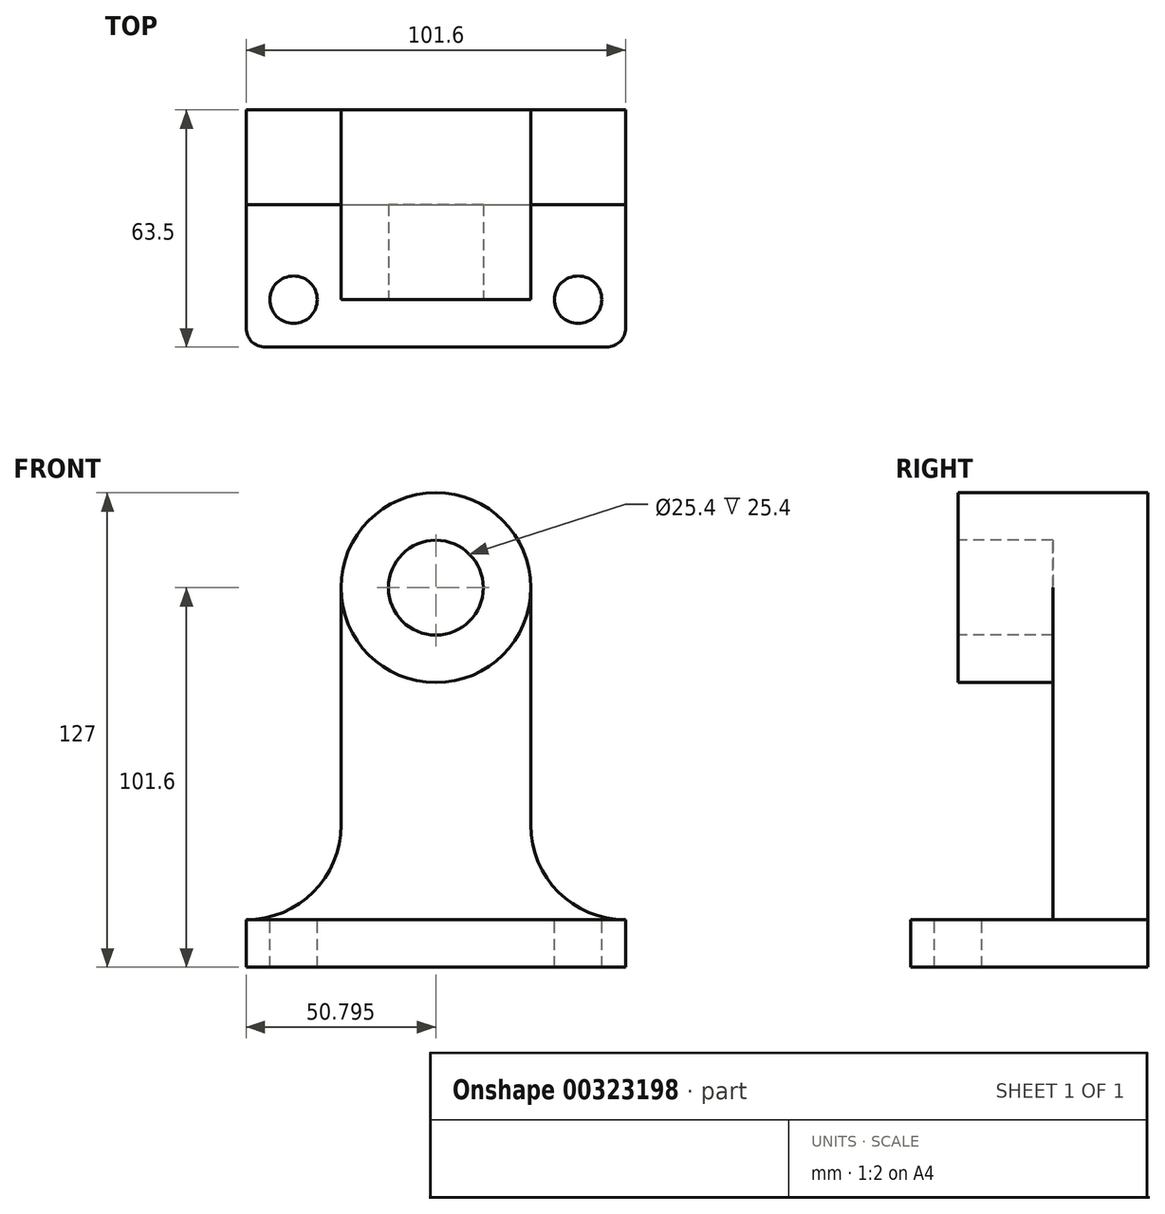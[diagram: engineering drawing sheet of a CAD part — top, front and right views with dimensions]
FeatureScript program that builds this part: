
annotation { "Feature Type Name" : "Feature", "Feature Type Description" : "" }
export const myFeature = defineFeature(function(context is Context, id is Id, definition is map)
    precondition{}
    {
        {
            var Q0;
            Q0=qCreatedBy(makeId("Top.planeOp"),FACE);
            var sketch = newSketch(context, id + "F0", { "sketchPlane" : qUnion([Q0])});
            skLineSegment(sketch, "E0", {"start": v(-42.13, 38.8) * mm, "end": v(59.47, 38.8) * mm});
            skLineSegment(sketch, "E1", {"start": v(59.47, 38.8) * mm, "end": v(59.47, -24.7) * mm});
            skLineSegment(sketch, "E2", {"start": v(59.47, -24.7) * mm, "end": v(-42.13, -24.7) * mm});
            skLineSegment(sketch, "E3", {"start": v(-42.13, -24.7) * mm, "end": v(-42.13, 38.8) * mm});
            skSolve(sketch);
        }
        {
            var Q0;
            Q0=makeQuery(id+"F0.imprint","IMPRINT",FACE,{"disambiguationData":[TD([[makeQuery(id+"F0.imprint","IMPRINT",EDGE,{"derivedFrom":sQuery(id+"F0.wireOp",EDGE,"E0")}),-1.0]])]});
            extrude(context, id + "F1", {"entities" : qUnion([Q0]), "depth" : 12.7 * mm});
        }
        {
            var Q0;
            Q0=makeQuery(id+"F1.opExtrude","SWEPT_EDGE",EDGE,{"disambiguationData":[OSD([sQuery(id+"F0.wireOp",EDGE,"E1"),sQuery(id+"F0.wireOp",EDGE,"E2")])]});
            var Q1;
            Q1=makeQuery(id+"F1.opExtrude","SWEPT_EDGE",EDGE,{"disambiguationData":[OSD([sQuery(id+"F0.wireOp",EDGE,"E2"),sQuery(id+"F0.wireOp",EDGE,"E3")])]});
            fillet(context, id + "F2", {"entities" : qUnion([Q0, Q1]), "radius" : 5.08 * mm, "tangentPropagation" : true, "allowEdgeOverflow" : false});
        }
        {
            var Q0;
            Q0=makeQuery(id+"F1.opExtrude","CAP_FACE",FACE,{"disambiguationData":[OSD([sQuery(id+"F0.wireOp",EDGE,"E0"),sQuery(id+"F0.wireOp",EDGE,"E1"),sQuery(id+"F0.wireOp",EDGE,"E2"),sQuery(id+"F0.wireOp",EDGE,"E3")])],"isStart":false});
            var sketch = newSketch(context, id + "F3", { "sketchPlane" : qUnion([Q0])});
            skLineSegment(sketch, "E4", {"start": v(-42.13, 38.8) * mm, "end": v(-42.13, 13.4) * mm});
            skLineSegment(sketch, "E5", {"start": v(59.47, 13.4) * mm, "end": v(59.47, 38.8) * mm});
            skLineSegment(sketch, "E6", {"start": v(59.47, 38.8) * mm, "end": v(-42.13, 38.8) * mm});
            skLineSegment(sketch, "E7", {"start": v(-42.13, 13.4) * mm, "end": v(59.47, 13.4) * mm});
            skSolve(sketch);
        }
        {
            var Q0;
            Q0=makeQuery(id+"F3.imprint","IMPRINT",FACE,{"disambiguationData":[TD([[makeQuery(id+"F3.imprint","IMPRINT",EDGE,{"derivedFrom":sQuery(id+"F3.wireOp",EDGE,"E4")}),-1.0]])]});
            extrude(context, id + "F4", {"entities" : qUnion([Q0]), "operationType" : NewBodyOperationType.ADD, "depth" : 63.5 * mm});
        }
        {
            var Q0;
            Q0=makeQuery(id+"F4.opExtrude","CAP_FACE",FACE,{"disambiguationData":[OSD([sQuery(id+"F3.wireOp",EDGE,"E4"),sQuery(id+"F3.wireOp",EDGE,"E5"),sQuery(id+"F3.wireOp",EDGE,"E6"),sQuery(id+"F3.wireOp",EDGE,"E7")])],"isStart":false});
            var sketch = newSketch(context, id + "F5", { "sketchPlane" : qUnion([Q0])});
            skLineSegment(sketch, "E8", {"start": v(-42.13, 13.4) * mm, "end": v(-16.73, 13.4) * mm});
            skLineSegment(sketch, "E9", {"start": v(-16.73, 13.4) * mm, "end": v(-16.73, 38.8) * mm});
            skLineSegment(sketch, "E10", {"start": v(-16.73, 38.8) * mm, "end": v(-42.13, 38.8) * mm});
            skLineSegment(sketch, "E11", {"start": v(-42.13, 38.8) * mm, "end": v(-42.13, 13.4) * mm});
            skLineSegment(sketch, "E12", {"start": v(59.47, 38.8) * mm, "end": v(34.07, 38.8) * mm});
            skLineSegment(sketch, "E13", {"start": v(34.07, 38.8) * mm, "end": v(34.07, 13.4) * mm});
            skLineSegment(sketch, "E14", {"start": v(34.07, 13.4) * mm, "end": v(59.47, 13.4) * mm});
            skLineSegment(sketch, "E15", {"start": v(59.47, 13.4) * mm, "end": v(59.47, 38.8) * mm});
            skSolve(sketch);
        }
        {
            var Q0;
            Q0=makeQuery(id+"F5.imprint","IMPRINT",FACE,{"disambiguationData":[TD([[makeQuery(id+"F5.imprint","IMPRINT",EDGE,{"derivedFrom":sQuery(id+"F5.wireOp",EDGE,"E8")}),1.0]])]});
            var Q1;
            Q1=makeQuery(id+"F5.imprint","IMPRINT",FACE,{"disambiguationData":[TD([[makeQuery(id+"F5.imprint","IMPRINT",EDGE,{"derivedFrom":sQuery(id+"F5.wireOp",EDGE,"E12")}),-1.0]])]});
            extrude(context, id + "F6", {"entities" : qUnion([Q0, Q1]), "operationType" : NewBodyOperationType.REMOVE, "oppositeDirection" : true, "depth" : 38.1 * mm});
        }
        {
            var Q0;
            Q0=makeQuery(id+"F4.opExtrude","SWEPT_FACE",FACE,{"disambiguationData":[OSD([sQuery(id+"F3.wireOp",EDGE,"E7")])]});
            var sketch = newSketch(context, id + "F7", { "sketchPlane" : qUnion([Q0])});
            skArc(sketch, "E16", {"start": v(34.07, 38.1) * mm, "mid": v(41.5, 20.14) * mm, "end": v(59.47, 12.7) * mm});
            skArc(sketch, "E17", {"start": v(-42.13, 12.7) * mm, "mid": v(-24.17, 20.14) * mm, "end": v(-16.73, 38.1) * mm});
            skLineSegment(sketch, "E18", {"start": v(-42.13, 12.7) * mm, "end": v(-42.13, 38.1) * mm});
            skLineSegment(sketch, "E19", {"start": v(-16.73, 38.1) * mm, "end": v(-42.13, 38.1) * mm});
            skLineSegment(sketch, "E20", {"start": v(34.07, 38.1) * mm, "end": v(59.47, 38.1) * mm});
            skLineSegment(sketch, "E21", {"start": v(59.47, 38.1) * mm, "end": v(59.47, 12.7) * mm});
            skSolve(sketch);
        }
        {
            var Q0;
            Q0=makeQuery(id+"F7.imprint","IMPRINT",FACE,{"disambiguationData":[TD([[makeQuery(id+"F7.imprint","IMPRINT",EDGE,{"derivedFrom":sQuery(id+"F7.wireOp",EDGE,"E17")}),1.0]])]});
            var Q1;
            Q1=makeQuery(id+"F7.imprint","IMPRINT",FACE,{"disambiguationData":[TD([[makeQuery(id+"F7.imprint","IMPRINT",EDGE,{"derivedFrom":sQuery(id+"F7.wireOp",EDGE,"E16")}),1.0]])]});
            extrude(context, id + "F8", {"entities" : qUnion([Q0, Q1]), "operationType" : NewBodyOperationType.REMOVE, "oppositeDirection" : true, "depth" : 25.4 * mm});
        }
        {
            var Q0;
            Q0=makeQuery(id+"F4.opExtrude","CAP_FACE",FACE,{"disambiguationData":[OSD([sQuery(id+"F3.wireOp",EDGE,"E4"),sQuery(id+"F3.wireOp",EDGE,"E5"),sQuery(id+"F3.wireOp",EDGE,"E6"),sQuery(id+"F3.wireOp",EDGE,"E7")])],"isStart":false});
            var sketch = newSketch(context, id + "F9", { "sketchPlane" : qUnion([Q0])});
            skLineSegment(sketch, "E22", {"start": v(34.07, 38.8) * mm, "end": v(-16.73, 38.8) * mm});
            skLineSegment(sketch, "E23", {"start": v(-16.73, 38.8) * mm, "end": v(-16.73, -12) * mm});
            skLineSegment(sketch, "E24", {"start": v(-16.73, -12) * mm, "end": v(34.07, -12) * mm});
            skLineSegment(sketch, "E25", {"start": v(34.07, -12) * mm, "end": v(34.07, 38.8) * mm});
            skSolve(sketch);
        }
        {
            var Q0;
            {var subQ2=sQuery(id+"F9.wireOp",EDGE,"E24");Q0=makeQuery(id+"F9.imprint","IMPRINT",FACE,{"disambiguationData":[TD([[makeQuery(id+"F9.imprint","IMPRINT",EDGE,{"derivedFrom":subQ2}),1.0]])]});}
            var Q1;
            {var subQ0=sQuery(id+"F9.wireOp",EDGE,"E22");Q1=makeQuery(id+"F9.imprint","IMPRINT",FACE,{"disambiguationData":[TD([[makeQuery(id+"F9.imprint","IMPRINT",EDGE,{"derivedFrom":subQ0}),-1.0]])]});}
            extrude(context, id + "F10", {"entities" : qUnion([Q0, Q1]), "operationType" : NewBodyOperationType.ADD, "depth" : 50.8 * mm});
        }
        {
            var Q0;
            Q0=makeQuery(id+"F10.opExtrude","SWEPT_FACE",FACE,{"disambiguationData":[OSD([sQuery(id+"F9.wireOp",EDGE,"E24")])]});
            var sketch = newSketch(context, id + "F11", { "sketchPlane" : qUnion([Q0])});
            skCircle(sketch, "E26", {"center": v(8.67, 101.6) * mm, "radius": 25.4 * mm});
            skPoint(sketch, "E26.centerSnap0", {"position": v(34.07, 101.6) * mm});
            skPoint(sketch, "E26.centerSnap1", {"position": v(8.67, 127) * mm});
            skLineSegment(sketch, "E27", {"start": v(-16.73, 101.6) * mm, "end": v(-16.73, 127) * mm});
            skLineSegment(sketch, "E28", {"start": v(-16.73, 127) * mm, "end": v(8.67, 127) * mm});
            skLineSegment(sketch, "E29", {"start": v(8.67, 127) * mm, "end": v(34.07, 127) * mm});
            skLineSegment(sketch, "E30", {"start": v(34.07, 127) * mm, "end": v(34.07, 101.6) * mm});
            skLineSegment(sketch, "E31", {"start": v(34.07, 76.2) * mm, "end": v(34.07, 101.6) * mm});
            skLineSegment(sketch, "E32", {"start": v(34.07, 76.2) * mm, "end": v(8.67, 76.2) * mm});
            skLineSegment(sketch, "E33", {"start": v(-16.73, 76.2) * mm, "end": v(8.67, 76.2) * mm});
            skLineSegment(sketch, "E34", {"start": v(-16.73, 76.2) * mm, "end": v(-16.73, 101.6) * mm});
            skSolve(sketch);
        }
        {
            var Q0;
            {var subQ2=sQuery(id+"F11.wireOp",EDGE,"E33");Q0=makeQuery(id+"F11.imprint","IMPRINT",FACE,{"disambiguationData":[TD([[makeQuery(id+"F11.imprint","IMPRINT",EDGE,{"derivedFrom":subQ2}),1.0]])]});}
            var Q1;
            {var subQ0=sQuery(id+"F11.wireOp",EDGE,"E31");Q1=makeQuery(id+"F11.imprint","IMPRINT",FACE,{"disambiguationData":[TD([[makeQuery(id+"F11.imprint","IMPRINT",EDGE,{"derivedFrom":subQ0}),-1.0]])]});}
            extrude(context, id + "F12", {"entities" : qUnion([Q0, Q1]), "operationType" : NewBodyOperationType.REMOVE, "oppositeDirection" : true, "depth" : 25.4 * mm});
        }
        {
            var Q0;
            Q0=makeQuery(id+"F10.opExtrude","SWEPT_FACE",FACE,{"disambiguationData":[OSD([sQuery(id+"F9.wireOp",EDGE,"E24")])]});
            var sketch = newSketch(context, id + "F13", { "sketchPlane" : qUnion([Q0])});
            skCircle(sketch, "E35", {"center": v(8.67, 101.6) * mm, "radius": 25.4 * mm});
            skLineSegment(sketch, "E36", {"start": v(-16.73, 101.6) * mm, "end": v(-16.73, 127) * mm});
            skLineSegment(sketch, "E37", {"start": v(-16.73, 127) * mm, "end": v(8.67, 127) * mm});
            skLineSegment(sketch, "E38", {"start": v(34.07, 127) * mm, "end": v(34.07, 101.6) * mm});
            skLineSegment(sketch, "E39", {"start": v(8.67, 127) * mm, "end": v(34.07, 127) * mm});
            skSolve(sketch);
        }
        {
            var Q0;
            {var subQ0=sQuery(id+"F13.wireOp",EDGE,"E36");Q0=makeQuery(id+"F13.imprint","IMPRINT",FACE,{"disambiguationData":[TD([[makeQuery(id+"F13.imprint","IMPRINT",EDGE,{"derivedFrom":subQ0}),1.0]])]});}
            var Q1;
            {var subQ0=sQuery(id+"F13.wireOp",EDGE,"E38");Q1=makeQuery(id+"F13.imprint","IMPRINT",FACE,{"disambiguationData":[TD([[makeQuery(id+"F13.imprint","IMPRINT",EDGE,{"derivedFrom":subQ0}),-1.0]])]});}
            extrude(context, id + "F14", {"entities" : qUnion([Q0, Q1]), "operationType" : NewBodyOperationType.REMOVE, "oppositeDirection" : true, "depth" : 50.8 * mm});
        }
        {
            var Q0;
            Q0=makeQuery(id+"F10.opExtrude","SWEPT_FACE",FACE,{"disambiguationData":[OSD([sQuery(id+"F9.wireOp",EDGE,"E24")])]});
            var sketch = newSketch(context, id + "F15", { "sketchPlane" : qUnion([Q0])});
            skCircle(sketch, "E40", {"center": v(8.67, 101.6) * mm, "radius": 12.7 * mm});
            skSolve(sketch);
        }
        {
            var Q0;
            Q0=makeQuery(id+"F15.imprint","IMPRINT",FACE,{"disambiguationData":[TD([[makeQuery(id+"F15.imprint","IMPRINT",EDGE,{"derivedFrom":sQuery(id+"F15.wireOp",EDGE,"E40")}),1.0]])]});
            extrude(context, id + "F16", {"entities" : qUnion([Q0]), "operationType" : NewBodyOperationType.REMOVE, "oppositeDirection" : true, "depth" : 25.4 * mm});
        }
        {
            var Q0;
            Q0=makeQuery(id+"F1.opExtrude","CAP_FACE",FACE,{"disambiguationData":[OSD([sQuery(id+"F0.wireOp",EDGE,"E0"),sQuery(id+"F0.wireOp",EDGE,"E1"),sQuery(id+"F0.wireOp",EDGE,"E2"),sQuery(id+"F0.wireOp",EDGE,"E3")])],"isStart":false});
            var sketch = newSketch(context, id + "F17", { "sketchPlane" : qUnion([Q0])});
            skCircle(sketch, "E41", {"center": v(-29.43, -12) * mm, "radius": 6.35 * mm});
            skCircle(sketch, "E42", {"center": v(46.77, -12) * mm, "radius": 6.35 * mm});
            skSolve(sketch);
        }
        {
            var Q0;
            Q0=makeQuery(id+"F17.imprint","IMPRINT",FACE,{"disambiguationData":[TD([[makeQuery(id+"F17.imprint","IMPRINT",EDGE,{"derivedFrom":sQuery(id+"F17.wireOp",EDGE,"E41")}),1.0]])]});
            var Q1;
            Q1=makeQuery(id+"F17.imprint","IMPRINT",FACE,{"disambiguationData":[TD([[makeQuery(id+"F17.imprint","IMPRINT",EDGE,{"derivedFrom":sQuery(id+"F17.wireOp",EDGE,"E42")}),1.0]])]});
            extrude(context, id + "F18", {"entities" : qUnion([Q0, Q1]), "operationType" : NewBodyOperationType.REMOVE, "oppositeDirection" : true, "depth" : 25.4 * mm});
        }
    });
